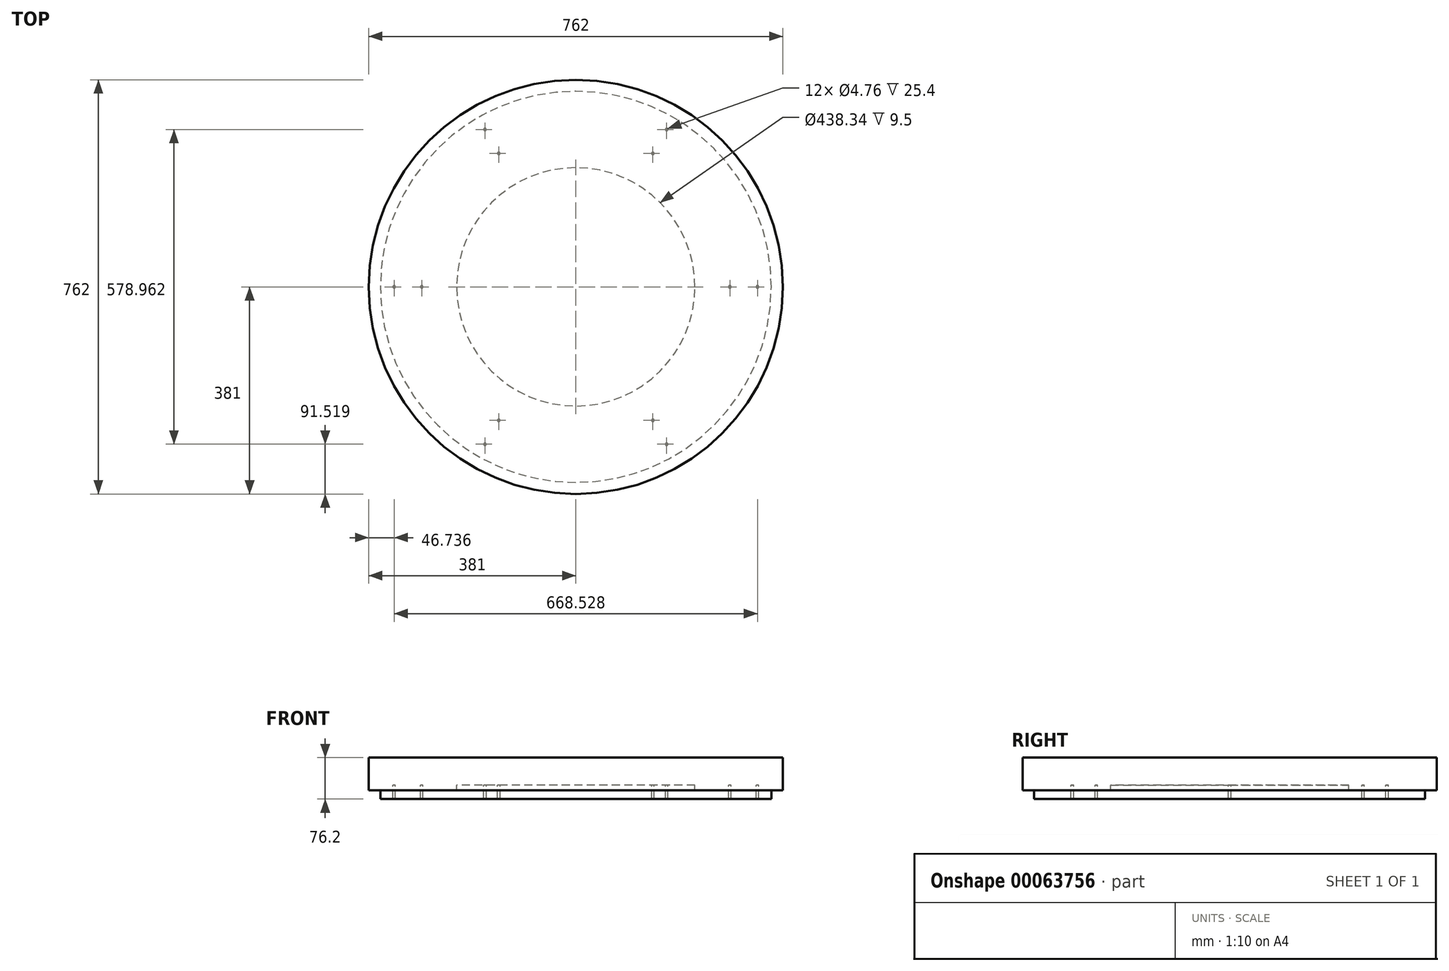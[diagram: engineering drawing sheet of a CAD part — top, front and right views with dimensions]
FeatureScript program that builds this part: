
annotation { "Feature Type Name" : "Feature", "Feature Type Description" : "" }
export const myFeature = defineFeature(function(context is Context, id is Id, definition is map)
    precondition{}
    {
        {
            assignVariable(context, id + "F0", {"name" : "H", "anyValue" : 15});
        }
        {
            assignVariable(context, id + "F1", {"name" : "S", "anyValue" : 6});
        }
        {
            var Q0;
            Q0=qCreatedBy(makeId("Top.planeOp"),FACE);
            var sketch = newSketch(context, id + "F2", { "sketchPlane" : qUnion([Q0])});
            skCircle(sketch, "E0", {"center": v(0, 0) * mm, "radius": 381 * mm});
            skCircle(sketch, "E1", {"center": v(0, 0) * mm, "radius": 368.3 * mm});
            skCircle(sketch, "E2.0", {"center": v(0, 0) * mm, "radius": 359.66 * mm});
            skSolve(sketch);
        }
        {
            var Q0;
            Q0=makeQuery(id+"F2.imprint","IMPRINT",FACE,{"disambiguationData":[TD([[makeQuery(id+"F2.imprint","IMPRINT",EDGE,{"derivedFrom":sQuery(id+"F2.wireOp",EDGE,"E1")}),1.0]])]});
            var Q1;
            Q1=sQuery(id+"F2.wireOp",EDGE,"E1");
            var Q2;
            Q2=sQuery(id+"F2.wireOp",EDGE,"E2.0");
            extrude(context, id + "F3", {"entities" : qUnion([Q0]), "surfaceEntities" : qUnion([Q1, Q2]), "depth" : (getVariable(context, 'H') - 5.5) * mm});
        }
        {
            var Q0;
            Q0=makeQuery(id+"F3.opExtrude","CAP_FACE",FACE,{"disambiguationData":[OSD([sQuery(id+"F2.wireOp",EDGE,"E1"),sQuery(id+"F2.wireOp",EDGE,"E2.0")])],"isStart":false});
            var sketch = newSketch(context, id + "F4", { "sketchPlane" : qUnion([Q0])});
            skCircle(sketch, "E3.0", {"center": v(0, 0) * mm, "radius": 359.66 * mm});
            skSolve(sketch);
        }
        {
            var Q0;
            Q0=qSketchRegion(id+"F4",true);
            extrude(context, id + "F5", {"entities" : qUnion([Q0]), "oppositeDirection" : true, "depth" : 25.4 * mm});
        }
        {
            var Q0;
            Q0=makeQuery(id+"F5.opExtrude","CAP_FACE",FACE,{"disambiguationData":[OSD([sQuery(id+"F4.wireOp",EDGE,"E3.0")])],"isStart":true});
            var sketch = newSketch(context, id + "F6", { "sketchPlane" : qUnion([Q0])});
            skLineSegment(sketch, "E4", {"start": v(-359.66, 0) * mm, "end": v(0, 0) * mm, "construction": true});
            skCircle(sketch, "E5.0", {"center": v(0, 0) * mm, "radius": 334.26 * mm, "construction": true});
            skCircle(sketch, "E6.0", {"center": v(0, 0) * mm, "radius": 283.46 * mm, "construction": true});
            skPoint(sketch, "E7", {"position": v(-334.26, 0) * mm});
            skPoint(sketch, "E8", {"position": v(-283.46, 0) * mm});
            skPoint(sketch, "E9.1.0", {"position": v(-141.73, -245.49) * mm});
            skPoint(sketch, "E9.1.1", {"position": v(-167.13, -289.48) * mm});
            skPoint(sketch, "E9.2.0", {"position": v(141.73, -245.49) * mm});
            skPoint(sketch, "E9.2.1", {"position": v(167.13, -289.48) * mm});
            skPoint(sketch, "E9.3.0", {"position": v(283.46, 0) * mm});
            skPoint(sketch, "E9.3.1", {"position": v(334.26, 0) * mm});
            skPoint(sketch, "E9.4.0", {"position": v(141.73, 245.49) * mm});
            skPoint(sketch, "E9.4.1", {"position": v(167.13, 289.48) * mm});
            skPoint(sketch, "E10.0.5.0", {"position": v(-141.73, 245.49) * mm});
            skPoint(sketch, "E10.1.5.0", {"position": v(-167.13, 289.48) * mm});
            skSolve(sketch);
        }
        {
            var Q0;
            Q0=sQuery(id+"F6.wireOp",VERTEX,"E7");
            var Q1;
            Q1=sQuery(id+"F6.wireOp",VERTEX,"E8");
            var Q2;
            Q2=sQuery(id+"F6.wireOp",VERTEX,"E9.4.1");
            var Q3;
            Q3=sQuery(id+"F6.wireOp",VERTEX,"E9.4.0");
            var Q4;
            Q4=sQuery(id+"F6.wireOp",VERTEX,"E9.3.0");
            var Q5;
            Q5=sQuery(id+"F6.wireOp",VERTEX,"E9.3.1");
            var Q6;
            Q6=sQuery(id+"F6.wireOp",VERTEX,"E9.2.0");
            var Q7;
            Q7=sQuery(id+"F6.wireOp",VERTEX,"E9.2.1");
            var Q8;
            Q8=sQuery(id+"F6.wireOp",VERTEX,"E9.1.1");
            var Q9;
            Q9=sQuery(id+"F6.wireOp",VERTEX,"E9.1.0");
            var Q10;
            Q10=sQuery(id+"F6.wireOp",VERTEX,"E10.0.5.0");
            var Q11;
            Q11=sQuery(id+"F6.wireOp",VERTEX,"E10.1.5.0");
            var Q12;
            Q12=makeQuery(id+"F5.opExtrude","SWEPT_BODY",BODY,{"disambiguationData":[OSD([sQuery(id+"F4.wireOp",EDGE,"E3.0")])]});
            hole(context, id + "F7", {"style" : HoleStyle.C_SINK, "holeDiameter" : 4.76 * mm, "cSinkDiameter" : 8.43 * mm, "endStyle" : HoleEndStyle.THROUGH, "locations" : qUnion([Q0, Q1, Q2, Q3, Q4, Q5, Q6, Q7, Q8, Q9, Q10, Q11]), "scope" : qUnion([Q12]), "cSinkAngle" : 90 * degree});
        }
        {
            var Q0;
            Q0=makeQuery(id+"F5.opExtrude","SWEPT_BODY",BODY,{"disambiguationData":[OSD([sQuery(id+"F4.wireOp",EDGE,"E3.0")])]});
            var Q1;
            Q1=qCreatedBy(makeId("Top.planeOp"),FACE);
            mirror(context, id + "F8", {"entities" : qUnion([Q0]), "mirrorPlane" : qUnion([Q1])});
        }
        {
            var Q0;
            Q0=makeQuery(id+"F8.opPattern","COPY",BODY,{"derivedFrom":makeQuery(id+"F5.opExtrude","SWEPT_BODY",BODY,{"disambiguationData":[OSD([sQuery(id+"F4.wireOp",EDGE,"E3.0")])]}),"instanceName":"1"});
            var Q1;
            Q1=makeQuery(id+"F5.opExtrude","CAP_FACE",FACE,{"disambiguationData":[OSD([sQuery(id+"F4.wireOp",EDGE,"E3.0")])],"isStart":true});
            transform(context, id + "F9", {"entities" : qUnion([Q0]), "transformType" : TransformType.TRANSLATION_3D, "dx" : 0 * mm, "dy" : 0 * mm, "dz" : (getVariable(context, 'H') - 5.5) * mm, "makeCopy" : false});
        }
        {
            var Q0;
            Q0=makeQuery(id+"F8.opPattern","COPY",FACE,{"derivedFrom":makeQuery(id+"F5.opExtrude","CAP_FACE",FACE,{"disambiguationData":[OSD([sQuery(id+"F4.wireOp",EDGE,"E3.0")])],"isStart":true}),"instanceName":"1"});
            var sketch = newSketch(context, id + "F10", { "sketchPlane" : qUnion([Q0])});
            skCircle(sketch, "E11.0", {"center": v(0, 0) * mm, "radius": 341.4 * mm, "construction": true});
            skCircle(sketch, "E12.0", {"center": v(0, 0) * mm, "radius": 304.9 * mm, "construction": true});
            skCircle(sketch, "E13.0", {"center": v(0, 0) * mm, "radius": 268.38 * mm, "construction": true});
            skLineSegment(sketch, "E14", {"start": v(0, 0) * mm, "end": v(0, 341.4) * mm, "construction": true});
            skLineSegment(sketch, "E15.0", {"start": v(22.23, 0) * mm, "end": v(22.23, 265.2) * mm, "construction": true});
            skLineSegment(sketch, "E16.0", {"start": v(-22.23, 0) * mm, "end": v(-22.23, 265.2) * mm, "construction": true});
            skPoint(sketch, "E17", {"position": v(-22.23, 304.08) * mm});
            skPoint(sketch, "E18", {"position": v(-22.23, 267.46) * mm});
            skPoint(sketch, "E19", {"position": v(22.23, 267.46) * mm});
            skPoint(sketch, "E20", {"position": v(22.23, 304.08) * mm});
            skPoint(sketch, "E21", {"position": v(22.23, 340.68) * mm});
            skPoint(sketch, "E22", {"position": v(-22.23, 340.68) * mm});
            skPoint(sketch, "E23.1.0", {"position": v(-261.24, 61.51) * mm});
            skPoint(sketch, "E23.1.1", {"position": v(-296.07, 72.83) * mm});
            skPoint(sketch, "E23.1.2", {"position": v(-330.88, 84.14) * mm});
            skPoint(sketch, "E23.1.3", {"position": v(-317.14, 126.41) * mm});
            skPoint(sketch, "E23.1.4", {"position": v(-282.33, 115.1) * mm});
            skPoint(sketch, "E23.1.5", {"position": v(-247.5, 103.79) * mm});
            skPoint(sketch, "E23.2.0", {"position": v(-139.23, -229.44) * mm});
            skPoint(sketch, "E23.2.1", {"position": v(-160.76, -259.07) * mm});
            skPoint(sketch, "E23.2.2", {"position": v(-182.27, -288.68) * mm});
            skPoint(sketch, "E23.2.3", {"position": v(-218.23, -262.56) * mm});
            skPoint(sketch, "E23.2.4", {"position": v(-196.72, -232.95) * mm});
            skPoint(sketch, "E23.2.5", {"position": v(-175.19, -203.32) * mm});
            skPoint(sketch, "E23.3.0", {"position": v(175.19, -203.32) * mm});
            skPoint(sketch, "E23.3.1", {"position": v(196.72, -232.95) * mm});
            skPoint(sketch, "E23.3.2", {"position": v(218.23, -262.56) * mm});
            skPoint(sketch, "E23.3.3", {"position": v(182.27, -288.68) * mm});
            skPoint(sketch, "E23.3.4", {"position": v(160.76, -259.07) * mm});
            skPoint(sketch, "E23.3.5", {"position": v(139.23, -229.44) * mm});
            skPoint(sketch, "E23.4.0", {"position": v(247.5, 103.79) * mm});
            skPoint(sketch, "E23.4.1", {"position": v(282.33, 115.1) * mm});
            skPoint(sketch, "E23.4.2", {"position": v(317.14, 126.41) * mm});
            skPoint(sketch, "E23.4.3", {"position": v(330.88, 84.14) * mm});
            skPoint(sketch, "E23.4.4", {"position": v(296.07, 72.83) * mm});
            skPoint(sketch, "E23.4.5", {"position": v(261.24, 61.51) * mm});
            skSolve(sketch);
        }
        {
            var Q0;
            Q0=sQuery(id+"F10.wireOp",VERTEX,"E22");
            var Q1;
            Q1=sQuery(id+"F10.wireOp",VERTEX,"E17");
            var Q2;
            Q2=sQuery(id+"F10.wireOp",VERTEX,"E18");
            var Q3;
            Q3=sQuery(id+"F10.wireOp",VERTEX,"E19");
            var Q4;
            Q4=sQuery(id+"F10.wireOp",VERTEX,"E20");
            var Q5;
            Q5=sQuery(id+"F10.wireOp",VERTEX,"E21");
            var Q6;
            Q6=sQuery(id+"F10.wireOp",VERTEX,"E23.4.0");
            var Q7;
            Q7=sQuery(id+"F10.wireOp",VERTEX,"E23.4.1");
            var Q8;
            Q8=sQuery(id+"F10.wireOp",VERTEX,"E23.4.2");
            var Q9;
            Q9=sQuery(id+"F10.wireOp",VERTEX,"E23.4.3");
            var Q10;
            Q10=sQuery(id+"F10.wireOp",VERTEX,"E23.4.4");
            var Q11;
            Q11=sQuery(id+"F10.wireOp",VERTEX,"E23.4.5");
            var Q12;
            Q12=sQuery(id+"F10.wireOp",VERTEX,"E23.3.0");
            var Q13;
            Q13=sQuery(id+"F10.wireOp",VERTEX,"E23.3.1");
            var Q14;
            Q14=sQuery(id+"F10.wireOp",VERTEX,"E23.3.2");
            var Q15;
            Q15=sQuery(id+"F10.wireOp",VERTEX,"E23.3.3");
            var Q16;
            Q16=sQuery(id+"F10.wireOp",VERTEX,"E23.3.4");
            var Q17;
            Q17=sQuery(id+"F10.wireOp",VERTEX,"E23.3.5");
            var Q18;
            Q18=sQuery(id+"F10.wireOp",VERTEX,"E23.2.2");
            var Q19;
            Q19=sQuery(id+"F10.wireOp",VERTEX,"E23.2.1");
            var Q20;
            Q20=sQuery(id+"F10.wireOp",VERTEX,"E23.2.0");
            var Q21;
            Q21=sQuery(id+"F10.wireOp",VERTEX,"E23.2.5");
            var Q22;
            Q22=sQuery(id+"F10.wireOp",VERTEX,"E23.2.4");
            var Q23;
            Q23=sQuery(id+"F10.wireOp",VERTEX,"E23.2.3");
            var Q24;
            Q24=sQuery(id+"F10.wireOp",VERTEX,"E23.1.0");
            var Q25;
            Q25=sQuery(id+"F10.wireOp",VERTEX,"E23.1.5");
            var Q26;
            Q26=sQuery(id+"F10.wireOp",VERTEX,"E23.1.1");
            var Q27;
            Q27=sQuery(id+"F10.wireOp",VERTEX,"E23.1.2");
            var Q28;
            Q28=sQuery(id+"F10.wireOp",VERTEX,"E23.1.3");
            var Q29;
            Q29=sQuery(id+"F10.wireOp",VERTEX,"E23.1.4");
            var Q30;
            Q30=makeQuery(id+"F8.opPattern","COPY",BODY,{"derivedFrom":makeQuery(id+"F5.opExtrude","SWEPT_BODY",BODY,{"disambiguationData":[OSD([sQuery(id+"F4.wireOp",EDGE,"E3.0")])]}),"instanceName":"1"});
            hole(context, id + "F11", {"style" : HoleStyle.SIMPLE, "holeDiameter" : 3.17 * mm, "endStyle" : HoleEndStyle.BLIND, "holeDepth" : 3.17 * mm, "locations" : qUnion([Q0, Q1, Q2, Q3, Q4, Q5, Q6, Q7, Q8, Q9, Q10, Q11, Q12, Q13, Q14, Q15, Q16, Q17, Q18, Q19, Q20, Q21, Q22, Q23, Q24, Q25, Q26, Q27, Q28, Q29]), "scope" : qUnion([Q30])});
        }
        {
            var Q0;
            Q0=makeQuery(id+"F8.opPattern","COPY",FACE,{"derivedFrom":makeQuery(id+"F5.opExtrude","CAP_FACE",FACE,{"disambiguationData":[OSD([sQuery(id+"F4.wireOp",EDGE,"E3.0")])],"isStart":false}),"instanceName":"1"});
            var sketch = newSketch(context, id + "F12", { "sketchPlane" : qUnion([Q0])});
            skCircle(sketch, "E24", {"center": v(0, 0) * mm, "radius": 219.17 * mm});
            skSolve(sketch);
        }
        {
            var Q0;
            Q0=qSketchRegion(id+"F12",true);
            extrude(context, id + "F13", {"entities" : qUnion([Q0]), "operationType" : NewBodyOperationType.REMOVE, "oppositeDirection" : true, "depth" : 25.4 * mm});
        }
        {
            var Q0;
            Q0=makeQuery(id+"F8.opPattern","COPY",FACE,{"derivedFrom":makeQuery(id+"F5.opExtrude","CAP_FACE",FACE,{"disambiguationData":[OSD([sQuery(id+"F4.wireOp",EDGE,"E3.0")])],"isStart":false}),"instanceName":"1"});
            var sketch = newSketch(context, id + "F14", { "sketchPlane" : qUnion([Q0])});
            skLineSegment(sketch, "E25", {"start": v(-334.26, 0) * mm, "end": v(-283.46, 0) * mm, "construction": true});
            skLineSegment(sketch, "E26.0", {"start": v(-359.66, 12.7) * mm, "end": v(-258.06, 12.7) * mm});
            skLineSegment(sketch, "E27.0", {"start": v(-359.66, -12.7) * mm, "end": v(-258.06, -12.7) * mm});
            skLineSegment(sketch, "E28", {"start": v(-359.66, -12.7) * mm, "end": v(-359.66, 12.7) * mm});
            skLineSegment(sketch, "E29", {"start": v(-258.06, -12.7) * mm, "end": v(-258.06, 12.7) * mm});
            skSolve(sketch);
        }
        {
            var Q0;
            Q0=qSketchRegion(id+"F14",true);
            extrude(context, id + "F15", {"entities" : qUnion([Q0]), "depth" : (getVariable(context, 'H') - 7.5) * mm});
        }
        {
            var Q0;
            Q0=makeQuery(id+"F15.opExtrude","SWEPT_BODY",BODY,{"disambiguationData":[OSD([sQuery(id+"F14.wireOp",EDGE,"E26.0"),sQuery(id+"F14.wireOp",EDGE,"E27.0"),sQuery(id+"F14.wireOp",EDGE,"E28"),sQuery(id+"F14.wireOp",EDGE,"E29")])]});
            var Q1;
            Q1=makeQuery(id+"F8.opPattern","COPY",EDGE,{"derivedFrom":makeQuery(id+"F5.opExtrude","CAP_EDGE",EDGE,{"disambiguationData":[OSD([sQuery(id+"F4.wireOp",EDGE,"E3.0")])],"isStart":false}),"instanceName":"1"});
            circularPattern(context, id + "F16", {"entities" : qUnion([Q0]), "axis" : qUnion([Q1]), "angle" : 360 * degree, "instanceCount" : getVariable(context, 'S'), "equalSpace" : true});
        }
        {
            var Q0;
            Q0=makeQuery(id+"F2.imprint","IMPRINT",FACE,{"disambiguationData":[TD([[makeQuery(id+"F2.imprint","IMPRINT",EDGE,{"derivedFrom":sQuery(id+"F2.wireOp",EDGE,"E0")}),1.0]])]});
            extrude(context, id + "F17", {"entities" : qUnion([Q0]), "depth" : (getVariable(context, 'H') - 5.5) * mm});
        }
        {
            var Q0;
            Q0=makeQuery(id+"F17.opExtrude","CAP_FACE",FACE,{"disambiguationData":[OSD([sQuery(id+"F2.wireOp",EDGE,"E0"),sQuery(id+"F2.wireOp",EDGE,"E1")])],"isStart":false});
            var sketch = newSketch(context, id + "F18", { "sketchPlane" : qUnion([Q0])});
            skCircle(sketch, "E30.0", {"center": v(0, 0) * mm, "radius": 381 * mm});
            skSolve(sketch);
        }
        {
            var Q0;
            Q0=qSketchRegion(id+"F18",true);
            extrude(context, id + "F19", {"entities" : qUnion([Q0]), "operationType" : NewBodyOperationType.ADD, "depth" : 50.8 * mm});
        }
    });
